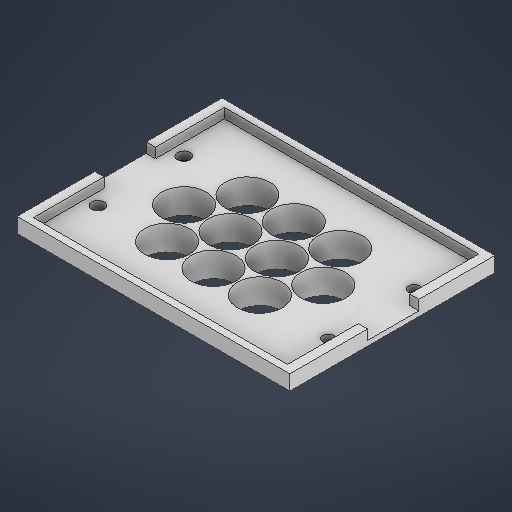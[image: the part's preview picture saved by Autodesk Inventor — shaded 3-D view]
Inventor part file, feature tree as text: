
AUTODESK INVENTOR PART (.ipt)
format: ipt  version: 2025.2 (Build 292293000, 293)  size: 613,376 bytes
history: native  units: mm
features: extrude x5, sketch x5, projected_geometry x3
ambient origin geometry x8: Origin, YZ Plane, XZ Plane, XY Plane, X Axis, Y Axis, Z Axis, Center Point
bodies: Solid1 (feature_tree)
feature tree (13):
  extrude  "Extrusion1"  Depth=29.0mm
  extrude  "Extrusion2"  Depth=29.0mm
  extrude  "Extrusion3"  Depth=29.0mm
  extrude  "Extrusion4"  Depth=29.0mm
  extrude  "Extrusion5"  Depth=5.0mm
  sketch  "Sketch1"  dims[d0=27.0mm d1=29.0mm]
  sketch  "Sketch2"  dims[d2=27.0mm d3=29.0mm]
  projected_geometry  "Projected Loop1"
  sketch  "Sketch3"  dims[d4=27.0mm d5=29.0mm]
  projected_geometry  "Projected Loop2"
  sketch  "Sketch4"  dims[d6=27.0mm d7=29.0mm]
  projected_geometry  "Projected Loop3"
  sketch  "Sketch5"  dims[d8=27.0mm d9=27.0mm d10=27.0mm d11=27.0mm d12=27.0mm d13=27.0mm d14=29.0mm d15=29.0mm d16=29.0mm d17=29.0mm d18=29.0mm d19=29.0mm d20=31.0mm d21=31.0mm d22=31.0mm d23=31.0mm d24=31.0mm d25=31.0mm d26=31.0mm d27=31.0mm d28=15.0mm d29=0.0mm d30=153.4mm d31=115.3mm d32=5.0mm d33=0.0mm d38=6.0mm d39=3.0mm d40=0.0mm d41=0.0mm d42=31.75mm d43=7.228mm d44=31.75mm d45=7.228mm d46=7.228mm d47=31.75mm d48=31.75mm d49=7.228mm d50=7.73mm d51=6.73mm d52=6.73mm d53=5.0mm d54=0.0mm d55=7.73mm d56=0.0mm d57=0.0mm]
